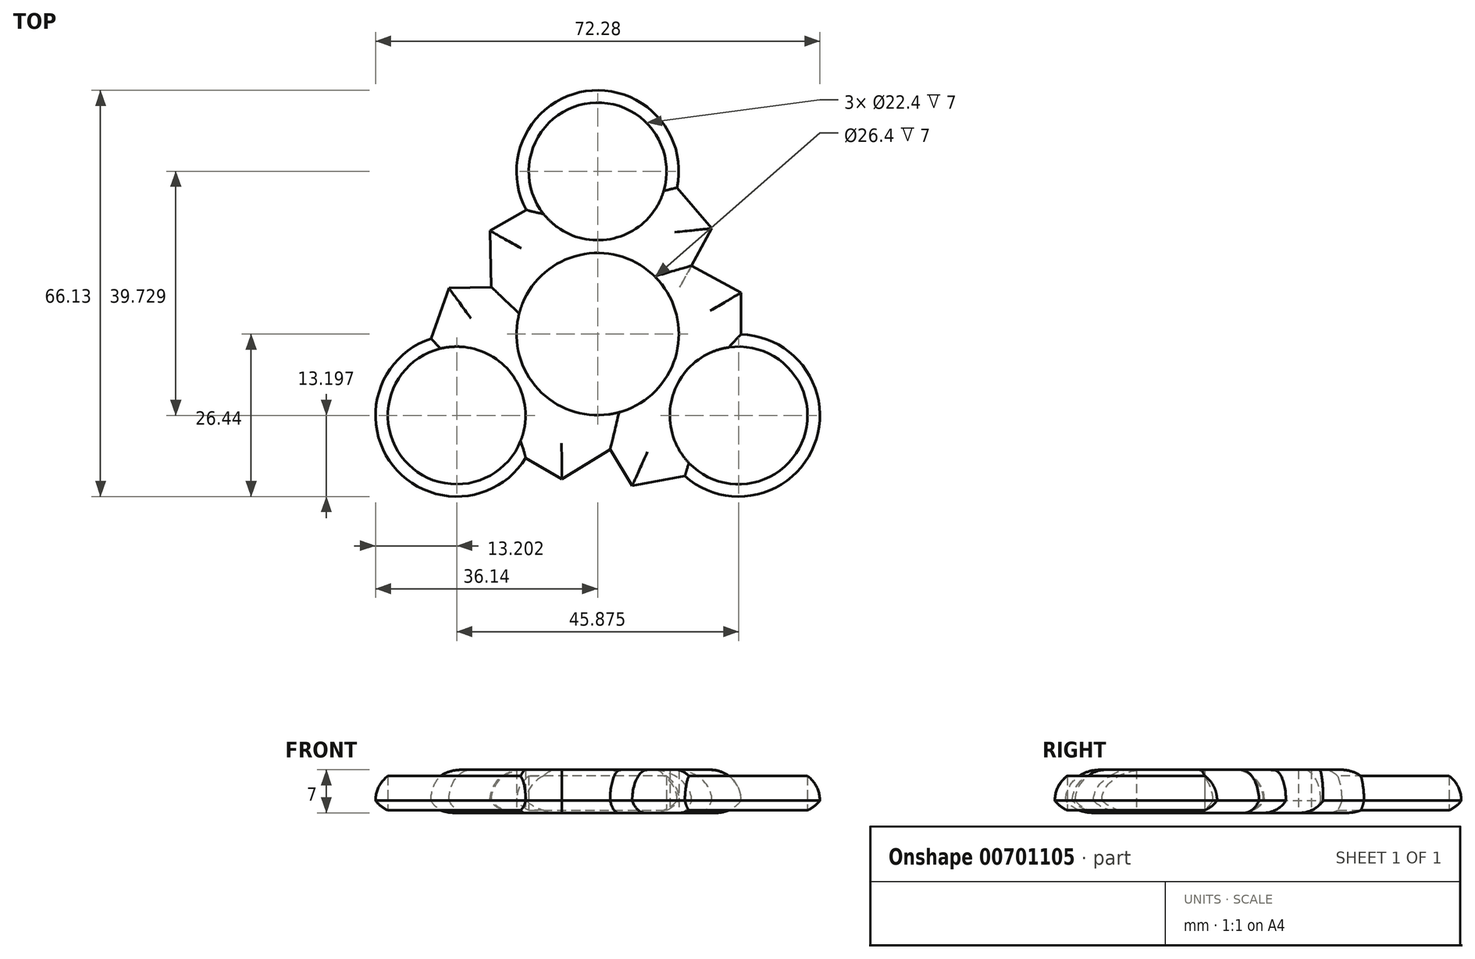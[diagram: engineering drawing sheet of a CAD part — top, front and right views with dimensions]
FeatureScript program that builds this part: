
annotation { "Feature Type Name" : "Feature", "Feature Type Description" : "" }
export const myFeature = defineFeature(function(context is Context, id is Id, definition is map)
    precondition{}
    {
        {
            var Q0;
            Q0=qCreatedBy(makeId("Top.planeOp"),FACE);
            var sketch = newSketch(context, id + "F0", { "sketchPlane" : qUnion([Q0])});
            skCircle(sketch, "E0", {"center": v(0, 0) * mm, "radius": 11.2 * mm});
            skCircle(sketch, "E1", {"center": v(0, 0) * mm, "radius": 13.2 * mm});
            skCircle(sketch, "E2", {"center": v(0, 26.49) * mm, "radius": 11.2 * mm});
            skCircle(sketch, "E3", {"center": v(0, 26.49) * mm, "radius": 13.2 * mm});
            skCircle(sketch, "E4.1.0", {"center": v(-22.94, -13.24) * mm, "radius": 11.2 * mm});
            skCircle(sketch, "E4.1.1", {"center": v(-22.94, -13.24) * mm, "radius": 13.2 * mm});
            skCircle(sketch, "E4.2.0", {"center": v(22.94, -13.24) * mm, "radius": 11.2 * mm});
            skCircle(sketch, "E4.2.1", {"center": v(22.94, -13.24) * mm, "radius": 13.2 * mm});
            skLineSegment(sketch, "E5", {"start": v(11.2, -23.16) * mm, "end": v(11.2, -19.27) * mm});
            skLineSegment(sketch, "E6", {"start": v(12.93, 23.85) * mm, "end": v(18.59, 17.2) * mm});
            skLineSegment(sketch, "E7", {"start": v(18.59, 17.2) * mm, "end": v(15.28, 11.15) * mm});
            skLineSegment(sketch, "E8", {"start": v(15.28, 11.15) * mm, "end": v(23.33, 6.76) * mm});
            skLineSegment(sketch, "E9", {"start": v(23.33, 6.76) * mm, "end": v(23.33, -0.05) * mm});
            skLineSegment(sketch, "E10.1.0", {"start": v(-17.3, 7.66) * mm, "end": v(-17.52, 16.82) * mm});
            skLineSegment(sketch, "E10.1.1", {"start": v(-27.12, -0.72) * mm, "end": v(-24.2, 7.5) * mm});
            skLineSegment(sketch, "E10.1.2", {"start": v(-24.2, 7.5) * mm, "end": v(-17.3, 7.66) * mm});
            skLineSegment(sketch, "E10.1.3", {"start": v(-17.52, 16.82) * mm, "end": v(-11.62, 20.23) * mm});
            skLineSegment(sketch, "E10.2.0", {"start": v(2.02, -18.81) * mm, "end": v(-5.8, -23.58) * mm});
            skLineSegment(sketch, "E10.2.1", {"start": v(14.19, -23.13) * mm, "end": v(5.61, -24.7) * mm});
            skLineSegment(sketch, "E10.2.2", {"start": v(5.61, -24.7) * mm, "end": v(2.02, -18.81) * mm});
            skLineSegment(sketch, "E10.2.3", {"start": v(-5.8, -23.58) * mm, "end": v(-11.7, -20.18) * mm});
            skSolve(sketch);
        }
        {
            var Q0;
            Q0 = qSketchRegion(id + "F0", true);
            extrude(context, id + "F1", {"entities" : qUnion([Q0]), "depth" : 7 * mm, "offsetDistance" : 25 * mm});
        }
        {
            var Q0;
            Q0=makeQuery(id+"F1.opExtrude","CAP_EDGE",EDGE,{"disambiguationData":[OSD([sQuery(id+"F0.wireOp",EDGE,"E4.2.1")])],"isStart":false});
            var Q1;
            Q1=makeQuery(id+"F1.opExtrude","CAP_EDGE",EDGE,{"disambiguationData":[OSD([sQuery(id+"F0.wireOp",EDGE,"E10.2.1")])],"isStart":false});
            var Q2;
            Q2=makeQuery(id+"F1.opExtrude","CAP_EDGE",EDGE,{"disambiguationData":[OSD([sQuery(id+"F0.wireOp",EDGE,"E10.2.2")])],"isStart":false});
            var Q3;
            Q3=makeQuery(id+"F1.opExtrude","CAP_EDGE",EDGE,{"disambiguationData":[OSD([sQuery(id+"F0.wireOp",EDGE,"E10.2.0")])],"isStart":false});
            var Q4;
            Q4=makeQuery(id+"F1.opExtrude","CAP_EDGE",EDGE,{"disambiguationData":[OSD([sQuery(id+"F0.wireOp",EDGE,"E10.2.3")])],"isStart":false});
            var Q5;
            Q5=makeQuery(id+"F1.opExtrude","CAP_EDGE",EDGE,{"disambiguationData":[OSD([sQuery(id+"F0.wireOp",EDGE,"E4.1.1")])],"isStart":false});
            var Q6;
            Q6=makeQuery(id+"F1.opExtrude","CAP_EDGE",EDGE,{"disambiguationData":[OSD([sQuery(id+"F0.wireOp",EDGE,"E9")])],"isStart":false});
            var Q7;
            Q7=makeQuery(id+"F1.opExtrude","CAP_EDGE",EDGE,{"disambiguationData":[OSD([sQuery(id+"F0.wireOp",EDGE,"E8")])],"isStart":false});
            var Q8;
            Q8=makeQuery(id+"F1.opExtrude","CAP_EDGE",EDGE,{"disambiguationData":[OSD([sQuery(id+"F0.wireOp",EDGE,"E7")])],"isStart":false});
            var Q9;
            Q9=makeQuery(id+"F1.opExtrude","CAP_EDGE",EDGE,{"disambiguationData":[OSD([sQuery(id+"F0.wireOp",EDGE,"E3")])],"isStart":false});
            var Q10;
            Q10=makeQuery(id+"F1.opExtrude","CAP_EDGE",EDGE,{"disambiguationData":[OSD([sQuery(id+"F0.wireOp",EDGE,"E10.1.3")])],"isStart":false});
            var Q11;
            Q11=makeQuery(id+"F1.opExtrude","CAP_EDGE",EDGE,{"disambiguationData":[OSD([sQuery(id+"F0.wireOp",EDGE,"E10.1.0")])],"isStart":false});
            var Q12;
            Q12=makeQuery(id+"F1.opExtrude","CAP_EDGE",EDGE,{"disambiguationData":[OSD([sQuery(id+"F0.wireOp",EDGE,"E10.1.2")])],"isStart":false});
            var Q13;
            Q13=makeQuery(id+"F1.opExtrude","CAP_EDGE",EDGE,{"disambiguationData":[OSD([sQuery(id+"F0.wireOp",EDGE,"E10.1.1")])],"isStart":false});
            var Q14;
            Q14=makeQuery(id+"F1.opExtrude","CAP_EDGE",EDGE,{"disambiguationData":[OSD([sQuery(id+"F0.wireOp",EDGE,"E6")])],"isStart":false});
            fillet(context, id + "F2", {"entities" : qUnion([Q0, Q1, Q2, Q3, Q4, Q5, Q6, Q7, Q8, Q9, Q10, Q11, Q12, Q13, Q14]), "radius" : 5 * mm, "tangentPropagation" : true, "allowEdgeOverflow" : false});
        }
        {
            var Q0;
            Q0=makeQuery(id+"F1.opExtrude","CAP_EDGE",EDGE,{"disambiguationData":[OSD([sQuery(id+"F0.wireOp",EDGE,"E10.2.3")])],"isStart":true});
            var Q1;
            Q1=makeQuery(id+"F1.opExtrude","CAP_EDGE",EDGE,{"disambiguationData":[OSD([sQuery(id+"F0.wireOp",EDGE,"E10.2.0")])],"isStart":true});
            var Q2;
            Q2=makeQuery(id+"F1.opExtrude","CAP_EDGE",EDGE,{"disambiguationData":[OSD([sQuery(id+"F0.wireOp",EDGE,"E10.1.2")])],"isStart":true});
            var Q3;
            Q3=makeQuery(id+"F1.opExtrude","CAP_EDGE",EDGE,{"disambiguationData":[OSD([sQuery(id+"F0.wireOp",EDGE,"E10.1.1")])],"isStart":true});
            var Q4;
            Q4=makeQuery(id+"F1.opExtrude","CAP_EDGE",EDGE,{"disambiguationData":[OSD([sQuery(id+"F0.wireOp",EDGE,"E9")])],"isStart":true});
            var Q5;
            Q5=makeQuery(id+"F1.opExtrude","CAP_EDGE",EDGE,{"disambiguationData":[OSD([sQuery(id+"F0.wireOp",EDGE,"E10.1.0")])],"isStart":true});
            var Q6;
            Q6=makeQuery(id+"F1.opExtrude","CAP_EDGE",EDGE,{"disambiguationData":[OSD([sQuery(id+"F0.wireOp",EDGE,"E8")])],"isStart":true});
            var Q7;
            Q7=makeQuery(id+"F1.opExtrude","CAP_EDGE",EDGE,{"disambiguationData":[OSD([sQuery(id+"F0.wireOp",EDGE,"E10.2.1")])],"isStart":true});
            var Q8;
            Q8=makeQuery(id+"F1.opExtrude","CAP_EDGE",EDGE,{"disambiguationData":[OSD([sQuery(id+"F0.wireOp",EDGE,"E6")])],"isStart":true});
            var Q9;
            Q9=makeQuery(id+"F1.opExtrude","CAP_EDGE",EDGE,{"disambiguationData":[OSD([sQuery(id+"F0.wireOp",EDGE,"E10.1.3")])],"isStart":true});
            var Q10;
            Q10=makeQuery(id+"F1.opExtrude","CAP_EDGE",EDGE,{"disambiguationData":[OSD([sQuery(id+"F0.wireOp",EDGE,"E10.2.2")])],"isStart":true});
            fillet(context, id + "F3", {"entities" : qUnion([Q0, Q1, Q2, Q3, Q4, Q5, Q6, Q7, Q8, Q9, Q10]), "radius" : 5 * mm, "tangentPropagation" : true, "allowEdgeOverflow" : false});
        }
        {
            var Q0;
            Q0=makeQuery(id+"F1.opExtrude","CAP_EDGE",EDGE,{"disambiguationData":[OSD([sQuery(id+"F0.wireOp",EDGE,"E4.1.1")])],"isStart":true});
            var Q1;
            Q1=makeQuery(id+"F1.opExtrude","CAP_EDGE",EDGE,{"disambiguationData":[OSD([sQuery(id+"F0.wireOp",EDGE,"E4.2.1")])],"isStart":true});
            var Q2;
            Q2=makeQuery(id+"F1.opExtrude","CAP_EDGE",EDGE,{"disambiguationData":[OSD([sQuery(id+"F0.wireOp",EDGE,"E3")])],"isStart":true});
            fillet(context, id + "F4", {"entities" : qUnion([Q0, Q1, Q2]), "radius" : 5 * mm, "tangentPropagation" : true, "allowEdgeOverflow" : false});
        }
    });
